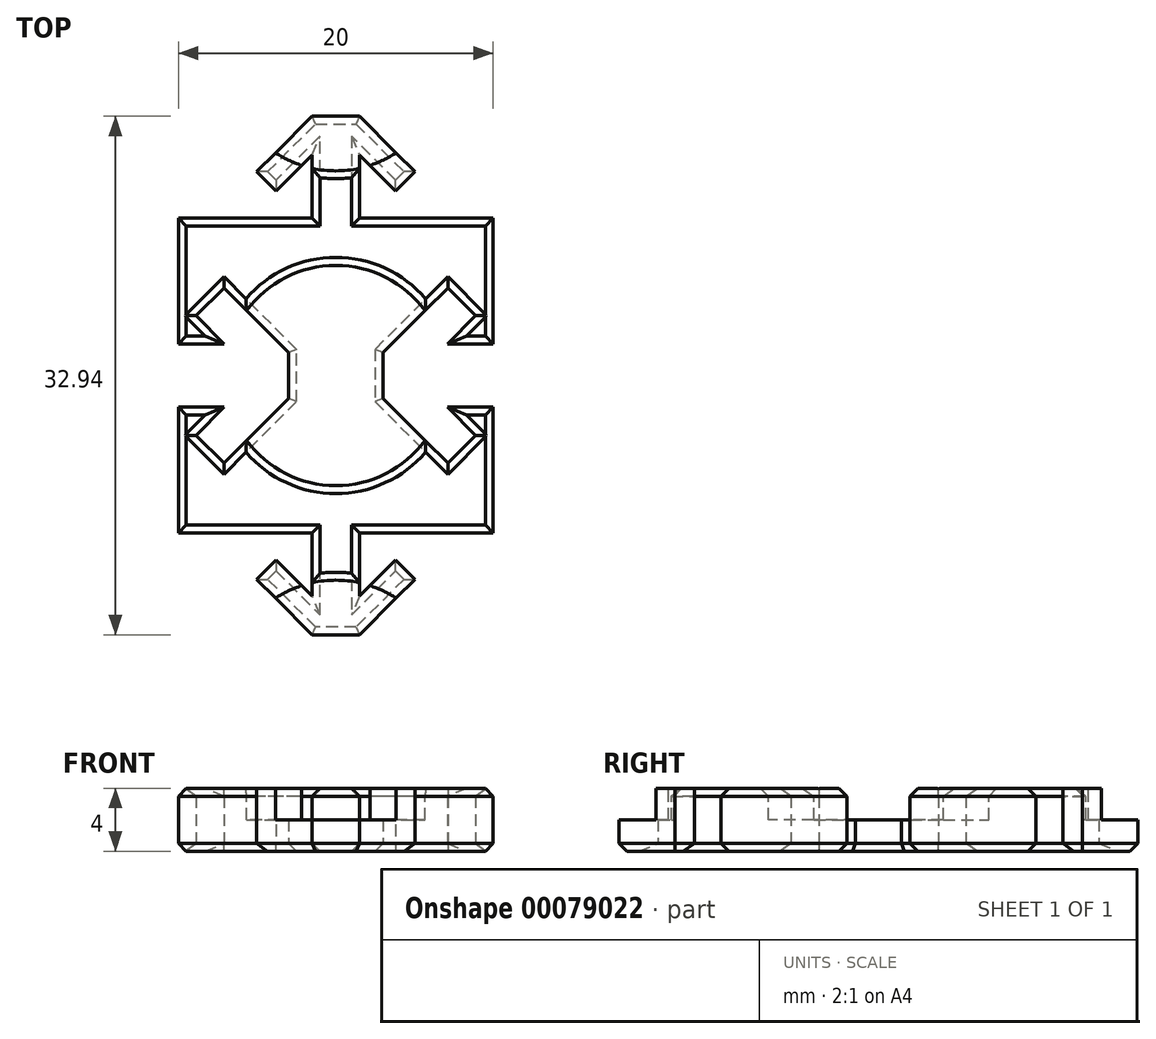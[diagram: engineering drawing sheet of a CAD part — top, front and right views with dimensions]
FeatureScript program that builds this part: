
annotation { "Feature Type Name" : "Feature", "Feature Type Description" : "" }
export const myFeature = defineFeature(function(context is Context, id is Id, definition is map)
    precondition{}
    {
        {
            var Q0;
            Q0=qCreatedBy(makeId("Top.planeOp"),FACE);
            var sketch = newSketch(context, id + "F0", { "sketchPlane" : qUnion([Q0])});
            skLineSegment(sketch, "E0.bottom", {"start": v(0, 0) * mm, "end": v(-10, 0) * mm});
            skLineSegment(sketch, "E0.top", {"start": v(0, 10) * mm, "end": v(-10, 10) * mm});
            skLineSegment(sketch, "E0.left", {"start": v(0, 0) * mm, "end": v(0, 10) * mm});
            skLineSegment(sketch, "E0.right", {"start": v(-10, 0) * mm, "end": v(-10, 10) * mm});
            skLineSegment(sketch, "E1", {"start": v(-1.5, 10) * mm, "end": v(-1.5, 14) * mm});
            skLineSegment(sketch, "E2", {"start": v(-1.5, 14) * mm, "end": v(-3.8, 11.7) * mm});
            skLineSegment(sketch, "E3", {"start": v(-3.8, 11.7) * mm, "end": v(-5.04, 12.94) * mm});
            skLineSegment(sketch, "E4", {"start": v(-5.04, 12.94) * mm, "end": v(-1.5, 16.47) * mm});
            skLineSegment(sketch, "E5", {"start": v(-1.5, 16.47) * mm, "end": v(0, 16.47) * mm});
            skLineSegment(sketch, "E6", {"start": v(-10, 1.5) * mm, "end": v(-5.87, 1.5) * mm, "construction": true});
            skLineSegment(sketch, "E7", {"start": v(-5.87, 1.5) * mm, "end": v(-8.17, 3.8) * mm, "construction": true});
            skLineSegment(sketch, "E8", {"start": v(-8.17, 3.8) * mm, "end": v(-7.11, 4.86) * mm, "construction": true});
            skLineSegment(sketch, "E9", {"start": v(-7.11, 4.86) * mm, "end": v(-3.75, 1.5) * mm, "construction": true});
            skLineSegment(sketch, "E10", {"start": v(-3.75, 1.5) * mm, "end": v(-3.75, 0) * mm, "construction": true});
            skLineSegment(sketch, "E11", {"start": v(0, 16.47) * mm, "end": v(0, 10) * mm});
            skLineSegment(sketch, "E12.1", {"start": v(-10, 2) * mm, "end": v(-7.08, 2) * mm});
            skLineSegment(sketch, "E12.2", {"start": v(-7.08, 2) * mm, "end": v(-8.88, 3.8) * mm});
            skLineSegment(sketch, "E12.3", {"start": v(-8.88, 3.8) * mm, "end": v(-7.11, 5.57) * mm});
            skLineSegment(sketch, "E12.4", {"start": v(-7.11, 5.57) * mm, "end": v(-3, 1.45) * mm});
            skLineSegment(sketch, "E13", {"start": v(-3, 1.45) * mm, "end": v(-3, 0) * mm});
            skSolve(sketch);
        }
        {
            var Q0;
            {var subQ2=sQuery(id+"F0.wireOp",EDGE,"E1");Q0=makeQuery(id+"F0.imprint","IMPRINT",FACE,{"disambiguationData":[TD([[makeQuery(id+"F0.imprint","IMPRINT",EDGE,{"derivedFrom":subQ2}),-1.0]])]});}
            var Q1;
            {var subQ0=sQuery(id+"F0.wireOp",EDGE,"E0.left");Q1=makeQuery(id+"F0.imprint","IMPRINT",FACE,{"disambiguationData":[TD([[makeQuery(id+"F0.imprint","IMPRINT",EDGE,{"derivedFrom":subQ0}),1.0]])]});}
            extrude(context, id + "F1", {"entities" : qUnion([Q0, Q1]), "depth" : 4 * mm});
        }
        {
            var Q0;
            Q0=makeQuery(id+"F1.opExtrude","SWEPT_BODY",BODY,{"disambiguationData":[OSD([sQuery(id+"F0.wireOp",EDGE,"E0.bottom"),sQuery(id+"F0.wireOp",EDGE,"E0.top"),sQuery(id+"F0.wireOp",EDGE,"E0.left"),sQuery(id+"F0.wireOp",EDGE,"E0.right"),sQuery(id+"F0.wireOp",EDGE,"E1"),sQuery(id+"F0.wireOp",EDGE,"E2"),sQuery(id+"F0.wireOp",EDGE,"E3"),sQuery(id+"F0.wireOp",EDGE,"E4"),sQuery(id+"F0.wireOp",EDGE,"E5"),sQuery(id+"F0.wireOp",EDGE,"E6"),sQuery(id+"F0.wireOp",EDGE,"E7"),sQuery(id+"F0.wireOp",EDGE,"E8"),sQuery(id+"F0.wireOp",EDGE,"E9"),sQuery(id+"F0.wireOp",EDGE,"E10"),sQuery(id+"F0.wireOp",EDGE,"E11")])]});
            var Q1;
            Q1=qCreatedBy(makeId("Right.planeOp"),FACE);
            mirror(context, id + "F2", {"operationType" : NewBodyOperationType.ADD, "entities" : qUnion([Q0]), "mirrorPlane" : qUnion([Q1])});
        }
        {
            var Q0;
            Q0=makeQuery(id+"F1.opExtrude","SWEPT_BODY",BODY,{"disambiguationData":[OSD([sQuery(id+"F0.wireOp",EDGE,"E0.bottom"),sQuery(id+"F0.wireOp",EDGE,"E0.top"),sQuery(id+"F0.wireOp",EDGE,"E0.left"),sQuery(id+"F0.wireOp",EDGE,"E0.right"),sQuery(id+"F0.wireOp",EDGE,"E1"),sQuery(id+"F0.wireOp",EDGE,"E2"),sQuery(id+"F0.wireOp",EDGE,"E3"),sQuery(id+"F0.wireOp",EDGE,"E4"),sQuery(id+"F0.wireOp",EDGE,"E5"),sQuery(id+"F0.wireOp",EDGE,"E6"),sQuery(id+"F0.wireOp",EDGE,"E7"),sQuery(id+"F0.wireOp",EDGE,"E8"),sQuery(id+"F0.wireOp",EDGE,"E9"),sQuery(id+"F0.wireOp",EDGE,"E10"),sQuery(id+"F0.wireOp",EDGE,"E11")])]});
            var Q1;
            Q1=qCreatedBy(makeId("Front.planeOp"),FACE);
            mirror(context, id + "F3", {"operationType" : NewBodyOperationType.ADD, "entities" : qUnion([Q0]), "mirrorPlane" : qUnion([Q1])});
        }
        {
            var Q0;
            {var subQ0=makeQuery(id+"F1.opExtrude","CAP_FACE",FACE,{"disambiguationData":[OSD([sQuery(id+"F0.wireOp",EDGE,"E0.bottom"),sQuery(id+"F0.wireOp",EDGE,"E0.top"),sQuery(id+"F0.wireOp",EDGE,"E0.left"),sQuery(id+"F0.wireOp",EDGE,"E0.right"),sQuery(id+"F0.wireOp",EDGE,"E1"),sQuery(id+"F0.wireOp",EDGE,"E2"),sQuery(id+"F0.wireOp",EDGE,"E3"),sQuery(id+"F0.wireOp",EDGE,"E4"),sQuery(id+"F0.wireOp",EDGE,"E5"),sQuery(id+"F0.wireOp",EDGE,"E11"),sQuery(id+"F0.wireOp",EDGE,"E12.0"),sQuery(id+"F0.wireOp",EDGE,"E12.1"),sQuery(id+"F0.wireOp",EDGE,"E12.2"),sQuery(id+"F0.wireOp",EDGE,"E12.3"),sQuery(id+"F0.wireOp",EDGE,"E12.4")])],"isStart":false});var subQ1=makeQuery(id+"F2.boolean.opBoolean","MERGE",FACE,{"derivedFrom":[subQ0,makeQuery(id+"F2.opPattern","COPY",FACE,{"derivedFrom":subQ0,"instanceName":"1"})]});Q0=makeQuery(id+"F3.boolean.opBoolean","MERGE",FACE,{"derivedFrom":[subQ1,makeQuery(id+"F3.opPattern","COPY",FACE,{"derivedFrom":subQ1,"instanceName":"1"})]});}
            var sketch = newSketch(context, id + "F4", { "sketchPlane" : qUnion([Q0])});
            skCircle(sketch, "E14", {"center": v(0, 0) * mm, "radius": 7 * mm});
            skCircle(sketch, "E15", {"center": v(0, 20) * mm, "radius": 7 * mm});
            skPoint(sketch, "E15.centerSnap0", {"position": v(0, 16.47) * mm});
            skCircle(sketch, "E16.MirrorC", {"center": v(0, -20) * mm, "radius": 7 * mm});
            skSolve(sketch);
        }
        {
            var Q0;
            Q0 = qSketchRegion(id + "F4", true);
            extrude(context, id + "F5", {"entities" : qUnion([Q0]), "operationType" : NewBodyOperationType.REMOVE, "oppositeDirection" : true, "depth" : 2 * mm});
        }
        {
            var Q0;
            {var subQ0=sQuery(id+"F0.wireOp",EDGE,"E0.top");var subQ1=makeQuery(id+"F1.opExtrude","SWEPT_FACE",FACE,{"disambiguationData":[OSD([subQ0])]});var subQ2=sQuery(id+"F0.wireOp",EDGE,"E12.4");var subQ4=sQuery(id+"F0.wireOp",EDGE,"E12.1");var subQ6=sQuery(id+"F0.wireOp",EDGE,"E12.3");var subQ8=sQuery(id+"F0.wireOp",EDGE,"E12.2");var subQ10=sQuery(id+"F0.wireOp",EDGE,"E0.right");var subQ12=sQuery(id+"F0.wireOp",EDGE,"E1");var subQ14=makeQuery(id+"F1.opExtrude","CAP_FACE",FACE,{"disambiguationData":[OSD([sQuery(id+"F0.wireOp",EDGE,"E0.bottom"),subQ0,sQuery(id+"F0.wireOp",EDGE,"E0.left"),subQ10,subQ12,sQuery(id+"F0.wireOp",EDGE,"E2"),sQuery(id+"F0.wireOp",EDGE,"E3"),sQuery(id+"F0.wireOp",EDGE,"E4"),sQuery(id+"F0.wireOp",EDGE,"E5"),sQuery(id+"F0.wireOp",EDGE,"E11"),subQ4,subQ8,subQ6,subQ2,sQuery(id+"F0.wireOp",EDGE,"E13")])],"isStart":false});var subQ15=makeQuery(id+"F2.boolean.opBoolean","MERGE",FACE,{"derivedFrom":[subQ14,makeQuery(id+"F2.opPattern","COPY",FACE,{"derivedFrom":subQ14,"instanceName":"1"})]});Q0=makeQuery(id+"F5.boolean.opBoolean","SPLIT",FACE,{"disambiguationData":[TD([makeQuery(id+"F3.opPattern","COPY",FACE,{"derivedFrom":subQ1,"instanceName":"1"})])],"derivedFrom":makeQuery(id+"F3.boolean.opBoolean","MERGE",FACE,{"derivedFrom":[subQ15,makeQuery(id+"F3.opPattern","COPY",FACE,{"derivedFrom":subQ15,"instanceName":"1"})]})});}
            var Q1;
            {var subQ0=sQuery(id+"F0.wireOp",EDGE,"E0.top");var subQ1=makeQuery(id+"F1.opExtrude","SWEPT_FACE",FACE,{"disambiguationData":[OSD([subQ0])]});var subQ2=sQuery(id+"F0.wireOp",EDGE,"E1");var subQ4=sQuery(id+"F0.wireOp",EDGE,"E12.1");var subQ6=sQuery(id+"F0.wireOp",EDGE,"E0.right");var subQ8=sQuery(id+"F0.wireOp",EDGE,"E12.4");var subQ10=sQuery(id+"F0.wireOp",EDGE,"E12.3");var subQ12=sQuery(id+"F0.wireOp",EDGE,"E12.2");var subQ14=makeQuery(id+"F1.opExtrude","CAP_FACE",FACE,{"disambiguationData":[OSD([sQuery(id+"F0.wireOp",EDGE,"E0.bottom"),subQ0,sQuery(id+"F0.wireOp",EDGE,"E0.left"),subQ6,subQ2,sQuery(id+"F0.wireOp",EDGE,"E2"),sQuery(id+"F0.wireOp",EDGE,"E3"),sQuery(id+"F0.wireOp",EDGE,"E4"),sQuery(id+"F0.wireOp",EDGE,"E5"),sQuery(id+"F0.wireOp",EDGE,"E11"),subQ4,subQ12,subQ10,subQ8,sQuery(id+"F0.wireOp",EDGE,"E13")])],"isStart":false});var subQ15=makeQuery(id+"F2.boolean.opBoolean","MERGE",FACE,{"derivedFrom":[subQ14,makeQuery(id+"F2.opPattern","COPY",FACE,{"derivedFrom":subQ14,"instanceName":"1"})]});Q1=makeQuery(id+"F5.boolean.opBoolean","SPLIT",FACE,{"disambiguationData":[TD([subQ1])],"derivedFrom":makeQuery(id+"F3.boolean.opBoolean","MERGE",FACE,{"derivedFrom":[subQ15,makeQuery(id+"F3.opPattern","COPY",FACE,{"derivedFrom":subQ15,"instanceName":"1"})]})});}
            var Q2;
            {var subQ0=makeQuery(id+"F1.opExtrude","CAP_FACE",FACE,{"disambiguationData":[OSD([sQuery(id+"F0.wireOp",EDGE,"E0.bottom"),sQuery(id+"F0.wireOp",EDGE,"E0.top"),sQuery(id+"F0.wireOp",EDGE,"E0.left"),sQuery(id+"F0.wireOp",EDGE,"E0.right"),sQuery(id+"F0.wireOp",EDGE,"E1"),sQuery(id+"F0.wireOp",EDGE,"E2"),sQuery(id+"F0.wireOp",EDGE,"E3"),sQuery(id+"F0.wireOp",EDGE,"E4"),sQuery(id+"F0.wireOp",EDGE,"E5"),sQuery(id+"F0.wireOp",EDGE,"E11"),sQuery(id+"F0.wireOp",EDGE,"E12.1"),sQuery(id+"F0.wireOp",EDGE,"E12.2"),sQuery(id+"F0.wireOp",EDGE,"E12.3"),sQuery(id+"F0.wireOp",EDGE,"E12.4"),sQuery(id+"F0.wireOp",EDGE,"E13")])],"isStart":true});var subQ1=makeQuery(id+"F2.boolean.opBoolean","MERGE",FACE,{"derivedFrom":[subQ0,makeQuery(id+"F2.opPattern","COPY",FACE,{"derivedFrom":subQ0,"instanceName":"1"})]});Q2=makeQuery(id+"F3.boolean.opBoolean","MERGE",FACE,{"derivedFrom":[subQ1,makeQuery(id+"F3.opPattern","COPY",FACE,{"derivedFrom":subQ1,"instanceName":"1"})]});}
            chamfer(context, id + "F6", {"entities" : qUnion([Q0, Q1, Q2]), "width" : 0.5 * mm, "tangentPropagation" : true});
        }
    });
